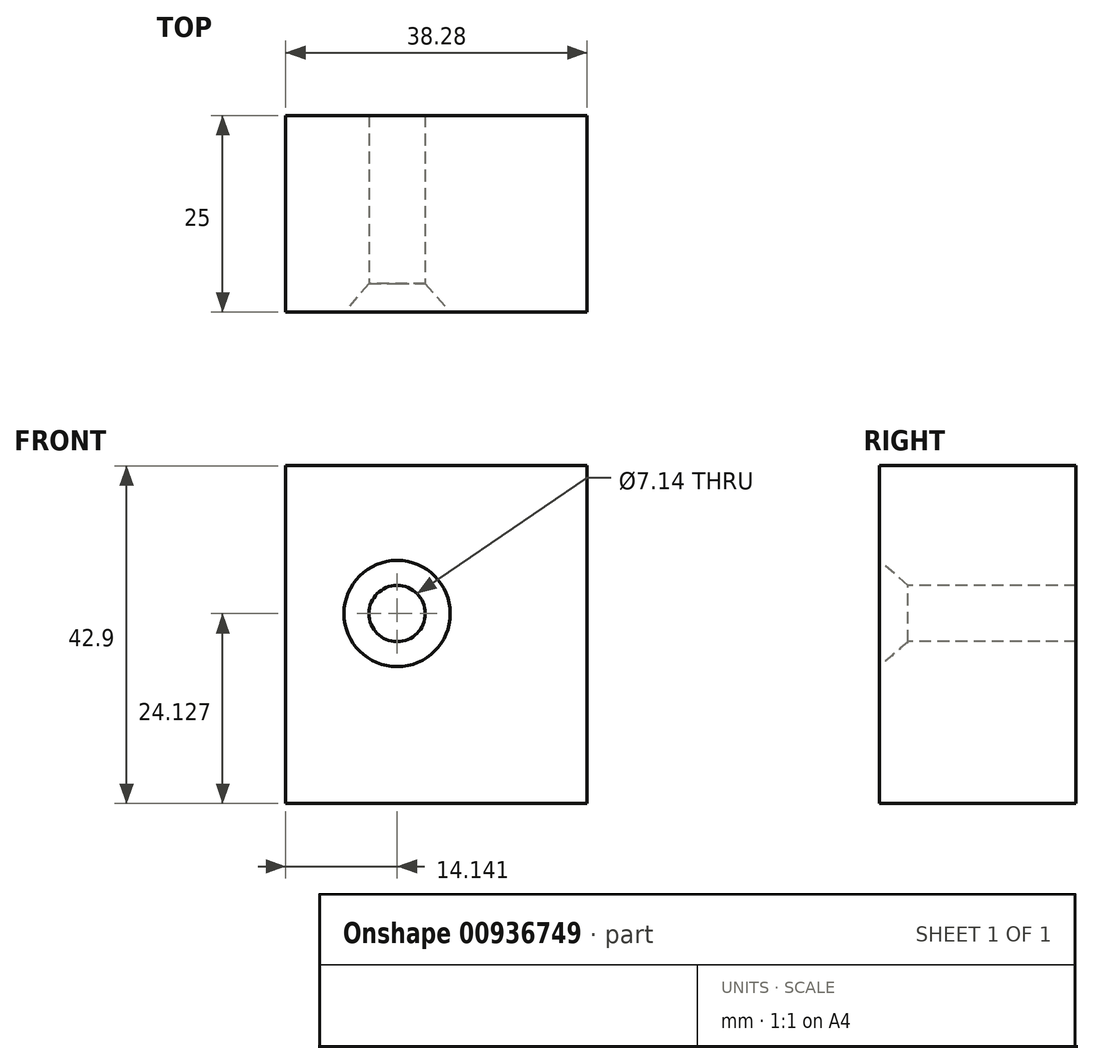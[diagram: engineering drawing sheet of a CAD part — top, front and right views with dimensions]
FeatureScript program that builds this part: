
annotation { "Feature Type Name" : "Feature", "Feature Type Description" : "" }
export const myFeature = defineFeature(function(context is Context, id is Id, definition is map)
    precondition{}
    {
        {
            var Q0;
            Q0=qCreatedBy(makeId("Front.planeOp"),FACE);
            var sketch = newSketch(context, id + "F0", { "sketchPlane" : qUnion([Q0])});
            skLineSegment(sketch, "E0.bottom", {"start": v(-81.68, 42.9) * mm, "end": v(-43.4, 42.9) * mm});
            skLineSegment(sketch, "E0.top", {"start": v(-81.68, 0) * mm, "end": v(-43.4, 0) * mm});
            skLineSegment(sketch, "E0.left", {"start": v(-81.68, 42.9) * mm, "end": v(-81.68, 0) * mm});
            skLineSegment(sketch, "E0.right", {"start": v(-43.4, 42.9) * mm, "end": v(-43.4, 0) * mm});
            skSolve(sketch);
        }
        {
            var Q0;
            Q0 = qSketchRegion(id + "F0", true);
            extrude(context, id + "F1", {"entities" : qUnion([Q0]), "depth" : 25 * mm, "offsetDistance" : 25 * mm});
        }
        {
            var Q0;
            Q0=makeQuery(id+"F1.opExtrude","CAP_FACE",FACE,{"disambiguationData":[OSD([sQuery(id+"F0.wireOp",EDGE,"E0.bottom"),sQuery(id+"F0.wireOp",EDGE,"E0.top"),sQuery(id+"F0.wireOp",EDGE,"E0.left"),sQuery(id+"F0.wireOp",EDGE,"E0.right")])],"isStart":false});
            var sketch = newSketch(context, id + "F2", { "sketchPlane" : qUnion([Q0])});
            skPoint(sketch, "E1", {"position": v(-67.54, 24.13) * mm});
            skSolve(sketch);
        }
        {
            var Q0;
            Q0=sQuery(id+"F2.wireOp",VERTEX,"E1");
            var Q1;
            Q1=makeQuery(id+"F1.opExtrude","SWEPT_BODY",BODY,{"disambiguationData":[OSD([sQuery(id+"F0.wireOp",EDGE,"E0.bottom"),sQuery(id+"F0.wireOp",EDGE,"E0.top"),sQuery(id+"F0.wireOp",EDGE,"E0.left"),sQuery(id+"F0.wireOp",EDGE,"E0.right")])]});
            hole(context, id + "F3", {"style" : HoleStyle.C_SINK, "endStyle" : HoleEndStyle.THROUGH, "standardTappedOrClearance" : lookupTablePath({ "fit" : "Normal (ASME)", "standard" : "ANSI", "size" : "1/4", "type" : "Clearance" }), "standardBlindInLast" : lookupTablePath({ "fit" : "Normal", "standard" : "ANSI", "engagement" : "75%", "pitch" : "20 tpi", "size" : "1/4", "type" : "Clearance & tapped" }), "holeDiameter" : 7.14 * mm, "cSinkDiameter" : 13.5 * mm, "cSinkAngle" : 82 * degree, "majorDiameter" : 5 * mm, "isTappedThrough" : true, "tappedDepth" : 12 * mm, "tapClearance" : 3, "locations" : qUnion([Q0]), "scope" : qUnion([Q1])});
        }
    });
